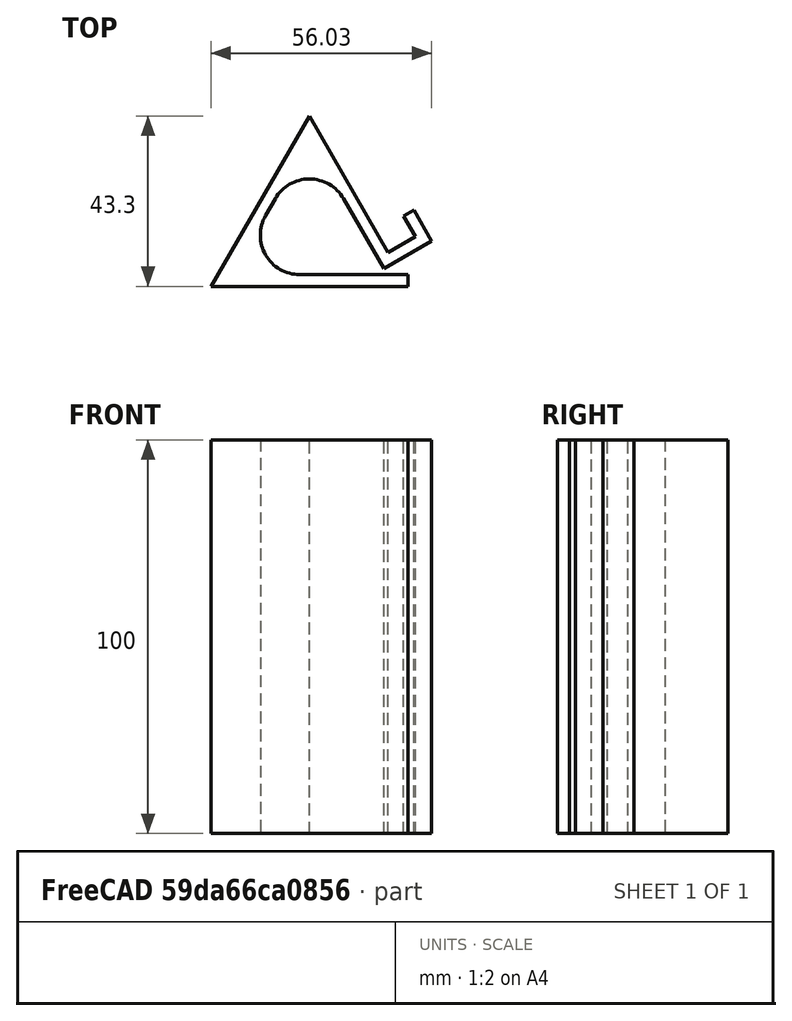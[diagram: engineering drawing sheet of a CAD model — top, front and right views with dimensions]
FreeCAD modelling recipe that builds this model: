
FCSTD DOCUMENT  (FreeCAD 0.22R38127 (Git))
Label: my phone stand
License: All rights reserved
LicenseURL: http://en.wikipedia.org/wiki/All_rights_reserved
objects: Sketcher::SketchObject×1, PartDesign::Pad×1, PartDesign::Body×1
note: 4 computed .brp shape members not serialized (recipe doc carries the construction recipe); baked Part::Feature solids carry a one-line shape summary decoded from their .brp

FEATURE [Sketcher::SketchObject] Sketch
  AttachmentSupport = -> [XY_Plane]
  FullyConstrained = true
  MapMode = 5
  sketch-geometry (18):
    g0: LineSegment StartX=50 StartY=0 StartZ=0 EndX=0 EndY=0 EndZ=0
    g1: LineSegment StartX=0 StartY=0 StartZ=0 EndX=25 EndY=43.3013 EndZ=0
    g2: LineSegment StartX=25 StartY=43.3013 StartZ=0 EndX=45 EndY=8.66025 EndZ=0
    g3: LineSegment StartX=45 StartY=8.66025 StartZ=0 EndX=51.9282 EndY=12.6603 EndZ=0
    g4: LineSegment StartX=51.9282 StartY=12.6603 StartZ=0 EndX=48.9282 EndY=17.8564 EndZ=0
    g5: LineSegment StartX=48.9282 StartY=17.8564 StartZ=0 EndX=51.5263 EndY=19.3564 EndZ=0
    g6: LineSegment StartX=51.5263 StartY=19.3564 StartZ=0 EndX=56.0263 EndY=11.5622 EndZ=0
    g7: LineSegment StartX=56.0263 StartY=11.5622 StartZ=0 EndX=43.9019 EndY=4.56218 EndZ=0
    g8: LineSegment StartX=22.5167 StartY=3 StartZ=0 EndX=50 EndY=3 EndZ=0
    g9: LineSegment StartX=50 StartY=3 StartZ=0 EndX=50 EndY=0 EndZ=0
    g10: LineSegment StartX=45 StartY=8.66025 StartZ=0 EndX=46.5 EndY=6.06218 EndZ=0
    g11: LineSegment StartX=13.8564 StartY=18 StartZ=0 EndX=16.3397 EndY=22.3013 EndZ=0
    g12: LineSegment StartX=33.6603 StartY=22.3013 StartZ=0 EndX=43.9019 EndY=4.56218 EndZ=0
    g13: ArcOfCircle CenterX=25 CenterY=17.3013 CenterZ=0 NormalX=0 NormalY=0 NormalZ=1 AngleXU=0 Radius=10 StartAngle=0.523599 EndAngle=2.61799
    g14: ArcOfCircle CenterX=22.5167 CenterY=13 CenterZ=0 NormalX=0 NormalY=0 NormalZ=1 AngleXU=0 Radius=10 StartAngle=2.61799 EndAngle=4.71239
    g15: GeomPoint X=5.19615 Y=3 Z=0
    g16: LineSegment StartX=12.5 StartY=21.6506 StartZ=0 EndX=15.0981 EndY=20.1506 EndZ=0
    g17: LineSegment StartX=45 StartY=8.66025 StartZ=0 EndX=42.4019 EndY=7.16025 EndZ=0
  constraints (49):
    c: PointOnObject(g0,g-1)
    c: Coincident(g0,g-1)
    c: Coincident(g0,g1)
    c: Coincident(g1,g2)
    c: Coincident(g2,g3)
    c: Coincident(g3,g4)
    c: Coincident(g4,g5)
    c: Coincident(g5,g6)
    c: Coincident(g6,g7)
    c: Horizontal(g8)
    c: Coincident(g8,g9)
    c: Coincident(g9,g0)
    c: Vertical(g9)
    c: Angle(g0,g1) = 1.0472
    c: Perpendicular(g5,g6)
    c: Perpendicular(g4,g5)
    c: Perpendicular(g6,g7)
    c: Perpendicular(g4,g3)
    c: Perpendicular(g2,g3)
    c: Angle(g1,g2) = 1.0472
    c: Distance(g5,g5) = 3
    c: DistanceY(g9,g9) = 3
    c: Coincident(g10,g2)
    c: PointOnObject(g10,g7)
    c: Perpendicular(g10,g7)
    c: Distance(g10,g10) = 3
    c: Distance(g3,g3) = 8
    c: Distance(g4,g4) = 6
    c: DistanceX(g0,g0) = 50
    c: Distance(g2,g2) = 40
    c: Coincident(g12,g7)
    c: Horizontal(g11,g12)
    c: Parallel(g11,g1)
    c: Tangent(g13,g12) = 1.5708
    c: Tangent(g13,g11) = 1.5708
    c: PointOnObject(g15,g11)
    c: PointOnObject(g15,g8)
    c: Tangent(g11,g14) = 1.5708
    c: Tangent(g8,g14) = -1.5708
    c: Radius(g14) = 10
    c: Radius(g13) = 10
    c: Symmetric(g1,g1,g16)
    c: Symmetric(g11,g11,g16)
    c: Distance(g16,g16) = 3
    c: Distance(g1,g1) = 50
    c: Coincident(g17,g2)
    c: PointOnObject(g17,g12)
    c: Perpendicular(g17,g12)
    c: Distance(g17,g17) = 3
FEATURE [PartDesign::Pad] Pad
  Direction = (0,0,1)
  Length = 100
  Length2 = 10
  Profile = -> Sketch
  ReferenceAxis = -> Sketch [N_Axis]
  Refine = true
  Suppressed = false
  Type = 0
FEATURE [PartDesign::Body] Body
  AllowCompound = false
  Group = -> [Sketch,Pad]
  Origin = -> Origin
  Tip = -> Pad
